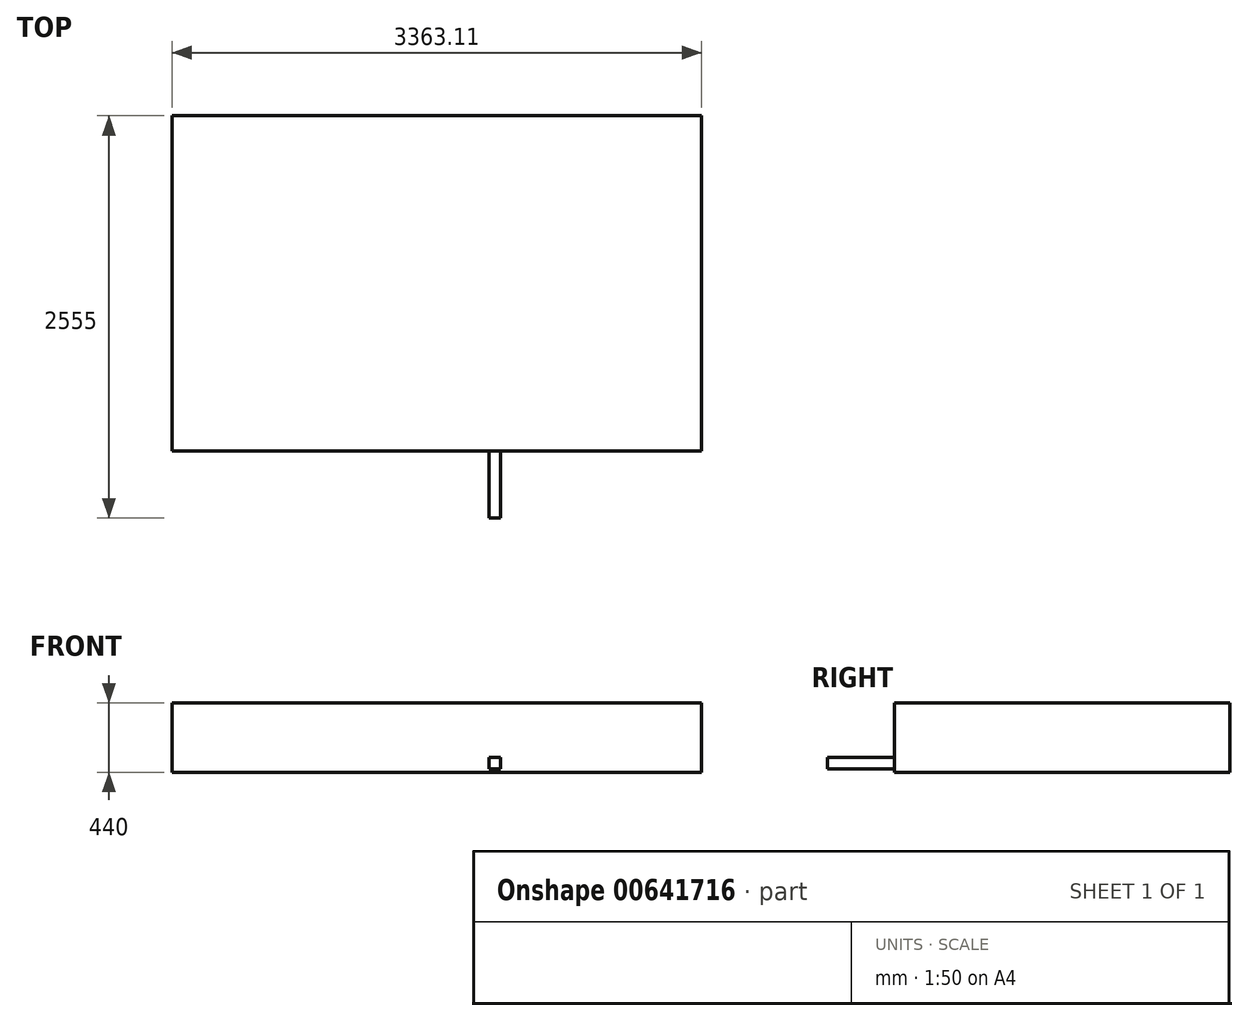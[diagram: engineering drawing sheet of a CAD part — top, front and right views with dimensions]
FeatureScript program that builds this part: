
annotation { "Feature Type Name" : "Feature", "Feature Type Description" : "" }
export const myFeature = defineFeature(function(context is Context, id is Id, definition is map)
    precondition{}
    {
        {
            var Q0;
            Q0=qCreatedBy(makeId("Front.planeOp"),FACE);
            var sketch = newSketch(context, id + "F0", { "sketchPlane" : qUnion([Q0])});
            skLineSegment(sketch, "E0.bottom", {"start": v(0, 0) * mm, "end": v(3363.1, 0) * mm});
            skLineSegment(sketch, "E0.top", {"start": v(0, -440) * mm, "end": v(3363.1, -440) * mm});
            skLineSegment(sketch, "E0.left", {"start": v(0, 0) * mm, "end": v(0, -440) * mm});
            skLineSegment(sketch, "E0.right", {"start": v(3363.1, 0) * mm, "end": v(3363.1, -440) * mm});
            skSolve(sketch);
        }
        {
            var Q0;
            Q0=makeQuery(id+"F0.imprint","IMPRINT",FACE,{"disambiguationData":[TD([[makeQuery(id+"F0.imprint","IMPRINT",EDGE,{"derivedFrom":sQuery(id+"F0.wireOp",EDGE,"E0.bottom")}),-1.0]])]});
            extrude(context, id + "F1", {"entities" : qUnion([Q0]), "oppositeDirection" : true, "depth" : 2130 * mm, "offsetDistance" : 25 * mm});
        }
        {
            var Q0;
            Q0=makeQuery(id+"F1.opExtrude","CAP_FACE",FACE,{"disambiguationData":[OSD([sQuery(id+"F0.wireOp",EDGE,"E0.bottom"),sQuery(id+"F0.wireOp",EDGE,"E0.top"),sQuery(id+"F0.wireOp",EDGE,"E0.left"),sQuery(id+"F0.wireOp",EDGE,"E0.right")])],"isStart":true});
            var sketch = newSketch(context, id + "F2", { "sketchPlane" : qUnion([Q0])});
            skLineSegment(sketch, "E1.bottom", {"start": v(2012.99, -345) * mm, "end": v(2087.99, -345) * mm});
            skLineSegment(sketch, "E1.top", {"start": v(2012.99, -420) * mm, "end": v(2087.99, -420) * mm});
            skLineSegment(sketch, "E1.left", {"start": v(2012.99, -345) * mm, "end": v(2012.99, -420) * mm});
            skLineSegment(sketch, "E1.right", {"start": v(2087.99, -345) * mm, "end": v(2087.99, -420) * mm});
            skSolve(sketch);
        }
        {
            var Q0;
            Q0 = qSketchRegion(id + "F2", true);
            extrude(context, id + "F3", {"entities" : qUnion([Q0]), "operationType" : NewBodyOperationType.ADD, "depth" : 425 * mm, "offsetDistance" : 25 * mm});
        }
    });
